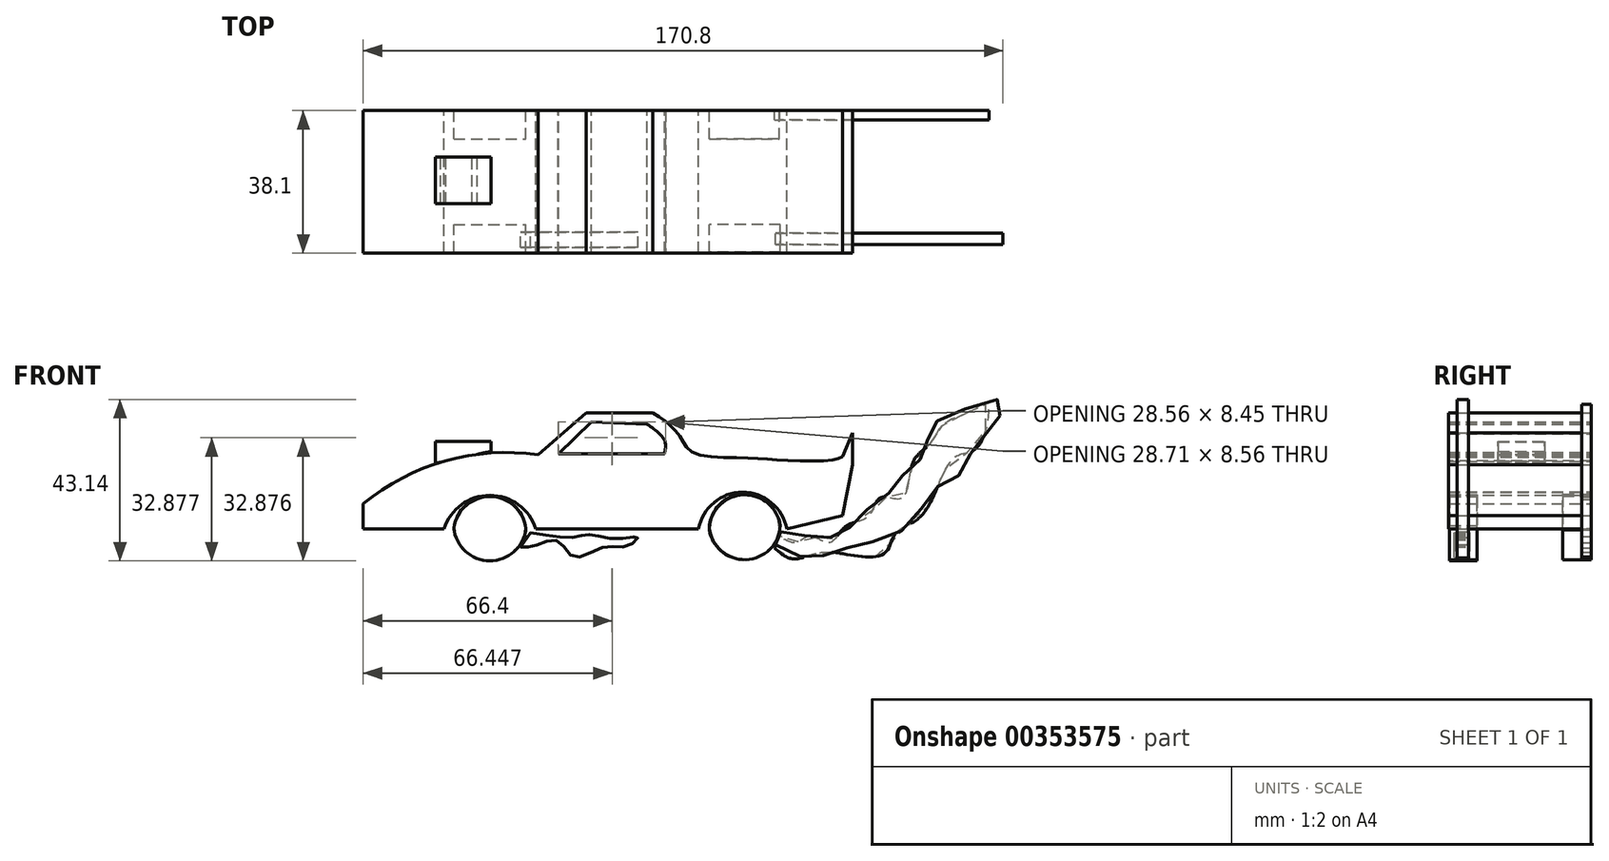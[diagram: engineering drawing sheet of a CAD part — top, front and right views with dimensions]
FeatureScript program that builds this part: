
annotation { "Feature Type Name" : "Feature", "Feature Type Description" : "" }
export const myFeature = defineFeature(function(context is Context, id is Id, definition is map)
    precondition{}
    {
        {
            var Q0;
            Q0=qCreatedBy(makeId("Front.planeOp"),FACE);
            var sketch = newSketch(context, id + "F0", { "sketchPlane" : qUnion([Q0])});
            skLineSegment(sketch, "E0", {"start": v(-56.25, -31.04) * mm, "end": v(-34.69, -31.04) * mm});
            skArc(sketch, "E1", {"start": v(-10.2, -31.04) * mm, "mid": v(-22.44, -22.07) * mm, "end": v(-34.69, -31.04) * mm});
            skLineSegment(sketch, "E2", {"start": v(-10.2, -31.04) * mm, "end": v(33.23, -31.04) * mm});
            skArc(sketch, "E3", {"start": v(56.84, -31.04) * mm, "mid": v(45.03, -21.23) * mm, "end": v(33.23, -31.04) * mm});
            skLineSegment(sketch, "E4", {"start": v(-56.25, -31.04) * mm, "end": v(-56.25, -24.34) * mm});
            skArc(sketch, "E5", {"start": v(-9.62, -11.22) * mm, "mid": v(-34.32, -12.87) * mm, "end": v(-56.25, -24.34) * mm});
            skLineSegment(sketch, "E6", {"start": v(-9.62, -11.22) * mm, "end": v(3.2, 0) * mm});
            skLineSegment(sketch, "E7", {"start": v(3.2, 0) * mm, "end": v(20.99, 0) * mm});
            skFitSpline(sketch, "E8", {"points": [v(20.99, 0) * mm, v(25.65, -3.35) * mm, v(28.86, -7.14) * mm, v(31.77, -10.64) * mm, v(45.47, -12.1) * mm, v(55.67, -12.68) * mm, v(68.79, -12.68) * mm, v(71.7, -11.8) * mm], "startDerivative": vector(38.88, -25.28) * mm, "endDerivative": vector(24.4, 11.03) * mm});
            skLineSegment(sketch, "E9", {"start": v(71.7, -11.8) * mm, "end": v(74.33, -5.4) * mm});
            skLineSegment(sketch, "E10", {"start": v(74.33, -5.4) * mm, "end": v(74.33, -13.85) * mm});
            skLineSegment(sketch, "E11", {"start": v(56.84, -31.04) * mm, "end": v(71.7, -27.54) * mm});
            skLineSegment(sketch, "E12", {"start": v(74.33, -13.85) * mm, "end": v(71.7, -27.54) * mm});
            skLineSegment(sketch, "E13", {"start": v(4.66, -2.48) * mm, "end": v(-4.08, -10.93) * mm});
            skLineSegment(sketch, "E14", {"start": v(-4.08, -10.93) * mm, "end": v(24.2, -10.93) * mm});
            skFitSpline(sketch, "E15", {"points": [v(24.2, -10.93) * mm, v(24.2, -7.43) * mm, v(19.53, -3.06) * mm], "startDerivative": vector(1.72, 8.36) * mm, "endDerivative": vector(-10.45, 7.43) * mm});
            skLineSegment(sketch, "E16", {"start": v(4.66, -2.48) * mm, "end": v(19.53, -3.06) * mm});
            skSolve(sketch);
        }
        {
            var Q0;
            Q0 = qSketchRegion(id + "F0", true);
            extrude(context, id + "F1", {"entities" : qUnion([Q0]), "depth" : 38.1 * mm});
        }
        {
            var Q0;
            Q0=qCreatedBy(makeId("Front.planeOp"),FACE);
            var sketch = newSketch(context, id + "F2", { "sketchPlane" : qUnion([Q0])});
            skArc(sketch, "E17", {"start": v(-12.82, -31.33) * mm, "mid": v(-22.3, -22.23) * mm, "end": v(-32.06, -31.04) * mm});
            skArc(sketch, "E18", {"start": v(-32.06, -31.04) * mm, "mid": v(-22.57, -39.34) * mm, "end": v(-12.82, -31.33) * mm});
            skArc(sketch, "E19", {"start": v(36.14, -31.33) * mm, "mid": v(45.47, -39.26) * mm, "end": v(54.8, -31.33) * mm});
            skArc(sketch, "E20", {"start": v(54.8, -31.33) * mm, "mid": v(45.47, -21.75) * mm, "end": v(36.14, -31.33) * mm});
            skSolve(sketch);
        }
        {
            var Q0;
            Q0 = qSketchRegion(id + "F2", true);
            extrude(context, id + "F3", {"entities" : qUnion([Q0]), "operationType" : NewBodyOperationType.ADD, "depth" : 7.62 * mm});
        }
        {
            var Q0;
            Q0=qCreatedBy(makeId("Front.planeOp"),FACE);
            var sketch = newSketch(context, id + "F4", { "sketchPlane" : qUnion([Q0])});
            skArc(sketch, "E21", {"start": v(36.14, -30.75) * mm, "mid": v(45.89, -39.26) * mm, "end": v(55.09, -30.17) * mm});
            skArc(sketch, "E22", {"start": v(-12.82, -30.89) * mm, "mid": v(-22.38, -22.43) * mm, "end": v(-32.06, -30.75) * mm});
            skArc(sketch, "E23", {"start": v(-32.06, -30.75) * mm, "mid": v(-22.5, -39.58) * mm, "end": v(-12.82, -30.89) * mm});
            skPoint(sketch, "E24.center.orphan", {"position": v(45.63, -30.89) * mm});
            skArc(sketch, "E25", {"start": v(55.09, -30.17) * mm, "mid": v(45.35, -21.96) * mm, "end": v(36.14, -30.75) * mm});
            skSolve(sketch);
        }
        {
            var Q0;
            Q0 = qSketchRegion(id + "F4", true);
            extrude(context, id + "F5", {"entities" : qUnion([Q0]), "depth" : 37.85 * mm, "hasSecondDirection" : true, "secondDirectionOppositeDirection" : false, "secondDirectionDepth" : 30.48 * mm});
        }
        {
            var Q0;
            Q0=qCreatedBy(makeId("Front.planeOp"),FACE);
            var sketch = newSketch(context, id + "F6", { "sketchPlane" : qUnion([Q0])});
            skLineSegment(sketch, "E26", {"start": v(-37.02, -13.55) * mm, "end": v(-37.02, -7.72) * mm});
            skLineSegment(sketch, "E27", {"start": v(-37.02, -7.72) * mm, "end": v(-22.15, -7.72) * mm});
            skLineSegment(sketch, "E28", {"start": v(-22.15, -7.72) * mm, "end": v(-22.15, -10.35) * mm});
            skArc(sketch, "E29", {"start": v(-22.15, -10.35) * mm, "mid": v(-29.59, -11.94) * mm, "end": v(-37.02, -13.55) * mm});
            skSolve(sketch);
        }
        {
            var Q0;
            Q0 = qSketchRegion(id + "F6", true);
            extrude(context, id + "F7", {"entities" : qUnion([Q0]), "operationType" : NewBodyOperationType.ADD, "depth" : 24.9 * mm, "hasSecondDirection" : true, "secondDirectionOppositeDirection" : false, "secondDirectionDepth" : 12.45 * mm});
        }
        {
            var Q0;
            Q0=makeQuery(id+"F7.opExtrude","SWEPT_FACE",FACE,{"disambiguationData":[OSD([sQuery(id+"F6.wireOp",EDGE,"E26")])]});
            shell(context, id + "F8", {"entities" : qUnion([Q0]), "thickness" : 0.05 * mm});
        }
        {
            var Q0;
            Q0=qCreatedBy(makeId("Front.planeOp"),FACE);
            var sketch = newSketch(context, id + "F9", { "sketchPlane" : qUnion([Q0])});
            skFitSpline(sketch, "E30", {"points": [v(-14.3, -35.9) * mm, v(-10.2, -35.43) * mm, v(-4.41, -34.22) * mm, v(0, -38.56) * mm, v(7.88, -35.9) * mm, v(14.14, -35.67) * mm, v(17.04, -33.26) * mm, v(11.73, -33.74) * mm, v(4.26, -32.53) * mm, v(0, -33.26) * mm, v(-11.64, -32.05) * mm], "startDerivative": vector(46.5, -0.5) * mm, "endDerivative": vector(-96.38, 16.54) * mm});
            skLineSegment(sketch, "E31", {"start": v(-11.64, -32.05) * mm, "end": v(-14.3, -35.9) * mm});
            skSolve(sketch);
        }
        {
            var Q0;
            Q0 = qSketchRegion(id + "F9", true);
            extrude(context, id + "F10", {"entities" : qUnion([Q0]), "depth" : 36.58 * mm, "hasSecondDirection" : true, "secondDirectionOppositeDirection" : false, "secondDirectionDepth" : 32.5 * mm});
        }
        {
            var Q0;
            Q0=qCreatedBy(makeId("Front.planeOp"),FACE);
            var sketch = newSketch(context, id + "F11", { "sketchPlane" : qUnion([Q0])});
            skFitSpline(sketch, "E32", {"points": [v(53.5, -36.15) * mm, v(58.56, -39.04) * mm, v(65.8, -37.35) * mm, v(75.67, -38.32) * mm, v(83.14, -37.35) * mm, v(86.03, -32.05) * mm, v(93.02, -27.23) * mm, v(101.46, -12.05) * mm, v(107.72, -9.16) * mm, v(110.38, 1.93) * mm, v(105.07, 0) * mm, v(98.33, -3.37) * mm, v(94.95, -8.43) * mm, v(90.61, -13.01) * mm, v(87.48, -22.9) * mm, v(81.94, -22.65) * mm, v(78.56, -27.71) * mm, v(72.54, -30.37) * mm, v(68.2, -34.7) * mm, v(63.14, -33.02) * mm, v(59.28, -34.7) * mm, v(54.95, -33.02) * mm], "startDerivative": vector(111.68, -96.5) * mm, "endDerivative": vector(-117.08, 77.5) * mm});
            skLineSegment(sketch, "E33", {"start": v(53.5, -36.15) * mm, "end": v(54.95, -33.02) * mm});
            skSolve(sketch);
        }
        {
            var Q0;
            Q0 = qSketchRegion(id + "F11", true);
            extrude(context, id + "F12", {"entities" : qUnion([Q0]), "depth" : 2.54 * mm});
        }
        {
            var Q0;
            Q0=qCreatedBy(makeId("Front.planeOp"),FACE);
            var sketch = newSketch(context, id + "F13", { "sketchPlane" : qUnion([Q0])});
            skFitSpline(sketch, "E34", {"points": [v(53.74, -35.19) * mm, v(62.66, -38.8) * mm, v(70.13, -36.87) * mm, v(78.8, -34.7) * mm, v(90.13, -29.4) * mm, v(96.4, -20.24) * mm, v(103.14, -16.39) * mm, v(106.76, -9.16) * mm, v(111.34, -4.58) * mm, v(114.23, 3.13) * mm, v(102.18, 0) * mm, v(95.2, -4.1) * mm, v(93.75, -10.6) * mm, v(88.44, -15.9) * mm, v(84.1, -21.45) * mm, v(76.64, -27.23) * mm, v(71.33, -32.53) * mm, v(63.14, -33.02) * mm, v(55.19, -31.81) * mm], "startDerivative": vector(154.18, -89) * mm, "endDerivative": vector(-142.53, 23.79) * mm});
            skLineSegment(sketch, "E35", {"start": v(55.19, -31.81) * mm, "end": v(53.74, -35.19) * mm});
            skSolve(sketch);
        }
        {
            var Q0;
            Q0 = qSketchRegion(id + "F13", true);
            extrude(context, id + "F14", {"entities" : qUnion([Q0]), "operationType" : NewBodyOperationType.ADD, "depth" : 35.81 * mm, "hasSecondDirection" : true, "secondDirectionOppositeDirection" : false, "secondDirectionDepth" : 32.77 * mm});
        }
    });
